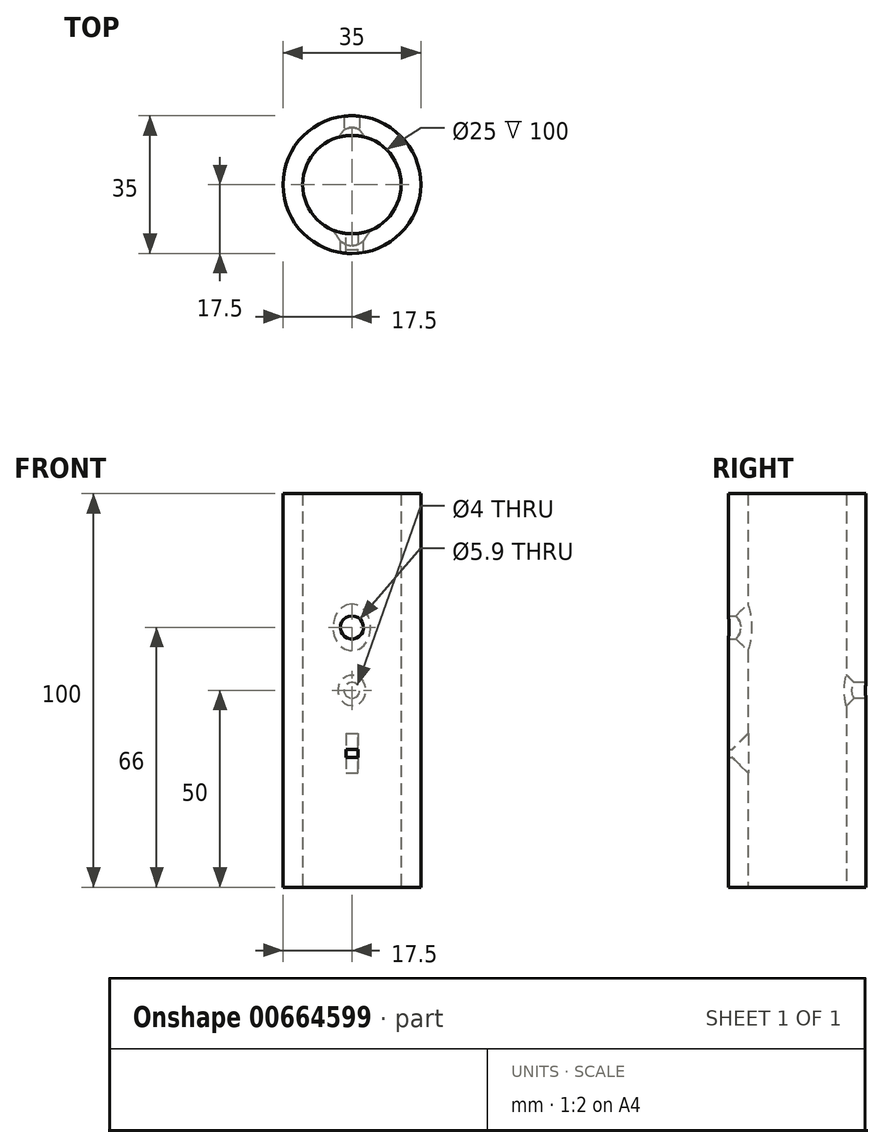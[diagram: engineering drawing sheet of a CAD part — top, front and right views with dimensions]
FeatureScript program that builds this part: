
annotation { "Feature Type Name" : "Feature", "Feature Type Description" : "" }
export const myFeature = defineFeature(function(context is Context, id is Id, definition is map)
    precondition{}
    {
        {
            var Q0;
            Q0=qCreatedBy(makeId("Top.planeOp"),FACE);
            var sketch = newSketch(context, id + "F0", { "sketchPlane" : qUnion([Q0])});
            skCircle(sketch, "E0", {"center": v(0, 0) * mm, "radius": 17.5 * mm});
            skCircle(sketch, "E1", {"center": v(0, 0) * mm, "radius": 12.5 * mm});
            skSolve(sketch);
        }
        {
            var Q0;
            Q0 = qSketchRegion(id + "F0", true);
            extrude(context, id + "F1", {"entities" : qUnion([Q0]), "depth" : 100 * mm, "offsetDistance" : 25 * mm});
        }
        {
            var Q0;
            Q0=qCreatedBy(makeId("Front.planeOp"),FACE);
            var sketch = newSketch(context, id + "F2", { "sketchPlane" : qUnion([Q0])});
            skCircle(sketch, "E2", {"center": v(0, 50) * mm, "radius": 2 * mm});
            skSolve(sketch);
        }
        {
            var Q0;
            Q0 = qSketchRegion(id + "F2", true);
            extrude(context, id + "F3", {"entities" : qUnion([Q0]), "operationType" : NewBodyOperationType.REMOVE, "oppositeDirection" : true, "depth" : 50 * mm, "offsetDistance" : 25 * mm});
        }
        {
            var Q0;
            Q0=qCreatedBy(makeId("Front.planeOp"),FACE);
            var sketch = newSketch(context, id + "F4", { "sketchPlane" : qUnion([Q0])});
            skLineSegment(sketch, "E3.bottom", {"start": v(-1.5, 35) * mm, "end": v(1.5, 35) * mm});
            skLineSegment(sketch, "E3.top", {"start": v(-1.5, 33) * mm, "end": v(1.5, 33) * mm});
            skLineSegment(sketch, "E3.left", {"start": v(-1.5, 35) * mm, "end": v(-1.5, 33) * mm});
            skLineSegment(sketch, "E3.right", {"start": v(1.5, 35) * mm, "end": v(1.5, 33) * mm});
            skCircle(sketch, "E4", {"center": v(0, 66) * mm, "radius": 2.95 * mm});
            skSolve(sketch);
        }
        {
            var Q0;
            Q0 = qSketchRegion(id + "F4", true);
            extrude(context, id + "F5", {"entities" : qUnion([Q0]), "operationType" : NewBodyOperationType.REMOVE, "depth" : 25 * mm, "offsetDistance" : 25 * mm});
        }
        {
            var Q0;
            Q0=makeQuery(id+"F3.boolean.opBoolean","INTERSECT",EDGE,{"derivedFrom":[makeQuery(id+"F1.opExtrude","SWEPT_FACE",FACE,{"disambiguationData":[OSD([sQuery(id+"F0.wireOp",EDGE,"E1")])]}),makeQuery(id+"F3.opExtrude","SWEPT_FACE",FACE,{"disambiguationData":[OSD([sQuery(id+"F2.wireOp",EDGE,"E2")])]})]});
            chamfer(context, id + "F6", {"entities" : qUnion([Q0]), "width" : 2 * mm, "tangentPropagation" : true});
        }
        {
            var Q0;
            Q0=makeQuery(id+"F5.boolean.opBoolean","INTERSECT",EDGE,{"derivedFrom":[makeQuery(id+"F1.opExtrude","SWEPT_FACE",FACE,{"disambiguationData":[OSD([sQuery(id+"F0.wireOp",EDGE,"E1")])]}),makeQuery(id+"F5.opExtrude","SWEPT_FACE",FACE,{"disambiguationData":[OSD([sQuery(id+"F4.wireOp",EDGE,"E4")])]})]});
            chamfer(context, id + "F7", {"entities" : qUnion([Q0]), "width" : 3 * mm, "tangentPropagation" : true});
        }
        {
            var Q0;
            Q0=makeQuery(id+"F5.boolean.opBoolean","INTERSECT",EDGE,{"derivedFrom":[makeQuery(id+"F1.opExtrude","SWEPT_FACE",FACE,{"disambiguationData":[OSD([sQuery(id+"F0.wireOp",EDGE,"E1")])]}),makeQuery(id+"F5.opExtrude","SWEPT_FACE",FACE,{"disambiguationData":[OSD([sQuery(id+"F4.wireOp",EDGE,"E3.top")])]})]});
            var Q1;
            Q1=makeQuery(id+"F5.boolean.opBoolean","INTERSECT",EDGE,{"derivedFrom":[makeQuery(id+"F1.opExtrude","SWEPT_FACE",FACE,{"disambiguationData":[OSD([sQuery(id+"F0.wireOp",EDGE,"E1")])]}),makeQuery(id+"F5.opExtrude","SWEPT_FACE",FACE,{"disambiguationData":[OSD([sQuery(id+"F4.wireOp",EDGE,"E3.bottom")])]})]});
            chamfer(context, id + "F8", {"entities" : qUnion([Q0, Q1]), "width" : 4 * mm, "tangentPropagation" : true});
        }
    });
